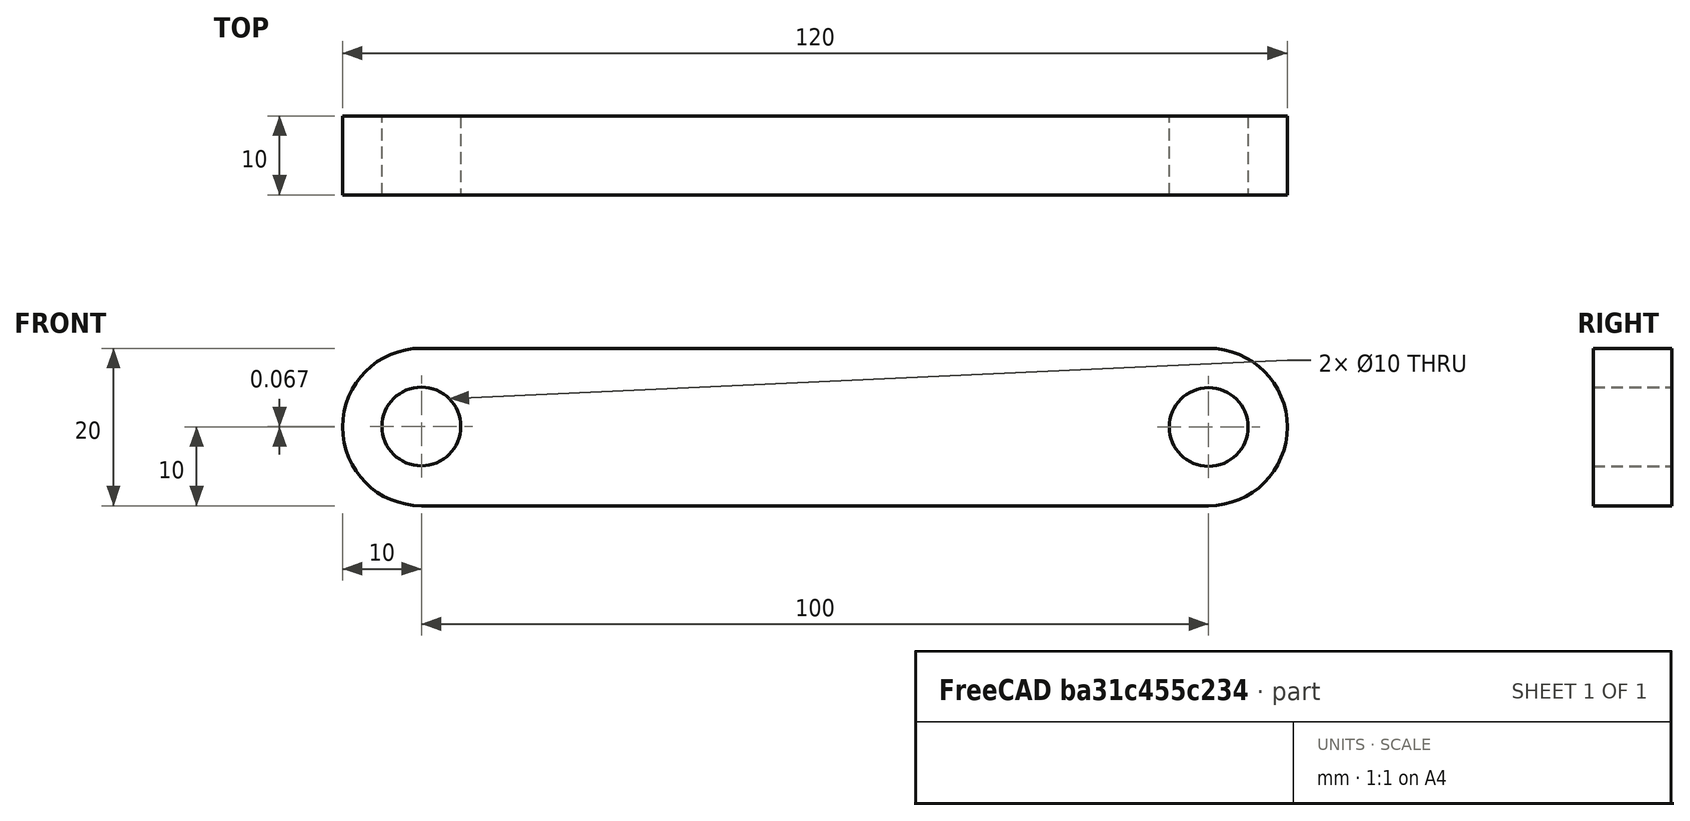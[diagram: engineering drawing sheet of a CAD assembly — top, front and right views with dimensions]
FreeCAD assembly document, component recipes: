
FREECAD ASSEMBLY — COMPONENT RECIPES ("Tuto1-002")

This assembly document has 2 components, labeled P0..P1 below (a component is one placed body or linked part). 1 of them carries a construction recipe — the FreeCAD feature program that regenerates the part from scratch, quoted from this document or its linked companion documents; the rest are supplied as boundary geometry only. No exploded tour is included for this assembly.
COMPONENT P0 — geometry summary ("Assembly"; no construction recipe available for this part):
  bounding box: 187.5 x 79.4 x 10.0 mm
  tessellated surface: 136 triangles
  volume: 269599466671506402234081112596510726420148261437092293409454295054376342095374861194592918402182409975518335451632640503398607845710483601597173416451913632217472958464 mm^3 (181082766403594481213695685495748729225116447471285457770859816284129900349645002397675206475258963498061897335469494717008462668751593952890036060026408880884940800% of its bounding box)
  symmetry: mirror-symmetric across its z mid-plane
COMPONENT P1 — recipe-attached ("Body", modeled in this document).
Construction recipe (the document's own serialized feature program — sketch geometry with constraints, then the solid features built on it; lengths are millimeters unless a unit is written):

FEATURE [PartDesign::CoordinateSystem] LCS_0
  AttacherType = Attacher::AttachEngine3D
  MapMode = 2
  Support = -> [X_Axis001]
FEATURE [Sketcher::SketchObject] Sketch
  FullyConstrained = false
  MapMode = 5
  Placement = pos=(0,0,0) rot=(1,0,0;1.5708rad)
  Support = -> [XZ_Plane001]
  sketch-geometry (6):
    g0: ArcOfCircle CenterX=0 CenterY=0 CenterZ=0 NormalX=0 NormalY=0 NormalZ=1 AngleXU=0 Radius=10 StartAngle=1.5708 EndAngle=4.71239
    g1: ArcOfCircle CenterX=100 CenterY=1.1e-15 CenterZ=0 NormalX=0 NormalY=0 NormalZ=1 AngleXU=0 Radius=10 StartAngle=4.71239 EndAngle=7.85398
    g2: LineSegment StartX=-1.8e-15 StartY=-10 StartZ=0 EndX=100 EndY=-10 EndZ=0
    g3: LineSegment StartX=100 StartY=10 StartZ=0 EndX=7.958e-13 EndY=10 EndZ=0
    g4: Circle CenterX=100 CenterY=1.1e-15 CenterZ=0 NormalX=0 NormalY=0 NormalZ=1 AngleXU=0 Radius=5
    g5: Circle CenterX=0 CenterY=0.067016 CenterZ=0 NormalX=0 NormalY=0 NormalZ=1 AngleXU=0 Radius=5
  constraints (11):
    c: Tangent(g0,g2) = -1.5708
    c: Tangent(g2,g1) = -1.5708
    c: Tangent(g1,g3) = -1.5708
    c: Tangent(g3,g0) = -1.5708
    c: Equal(g0,g1)
    c: Horizontal(g2)
    c: Coincident(g0,g-1)
    c: Coincident(g4,g1)
    c: PointOnObject(g5,g-2)
    c: Radius(g5) = 5
    c: DistanceX(g5,g1) = 100
FEATURE [PartDesign::Pad] Pad
  Direction = (0,-1,-2e-16)
  Length = 10
  Length2 = 10
  Placement = pos=(0,0,0) rot=(1,0,0;1.5708rad)
  Profile = -> Sketch
  ReferenceAxis = -> Sketch [N_Axis]
  Type = 0
FEATURE [PartDesign::Body] Body
  Group = -> [LCS_0,Sketch,Pad]
  Origin = -> Origin001
  Tip = -> Pad
PROVENANCE & LICENSES
A FreeCAD (.FCStd) document from a public repository crawl; recipes are the document's own serialized feature recipes (and, for linked parts, companion documents' recipes).
License: as declared in the source repository (recorded in the dataset sidecar).
